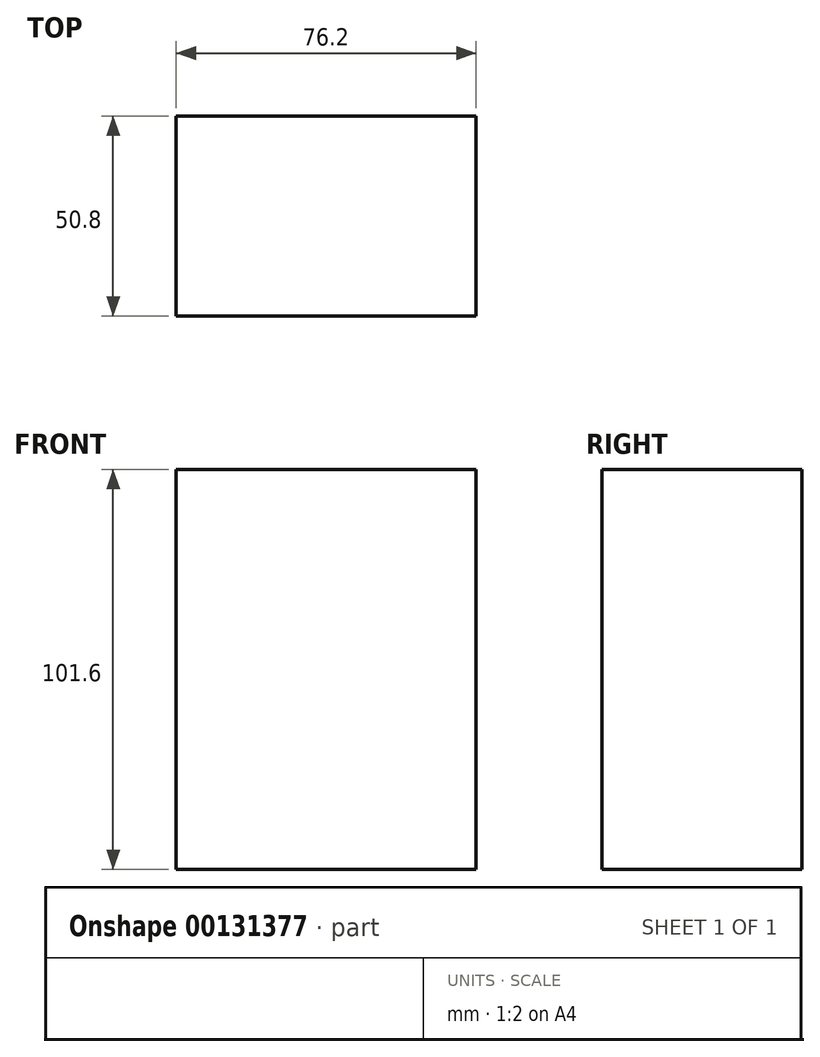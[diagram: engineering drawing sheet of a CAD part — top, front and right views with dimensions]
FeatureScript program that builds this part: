
annotation { "Feature Type Name" : "Feature", "Feature Type Description" : "" }
export const myFeature = defineFeature(function(context is Context, id is Id, definition is map)
    precondition{}
    {
        {
            var Q0;
            Q0=qCreatedBy(makeId("Front.planeOp"),FACE);
            var sketch = newSketch(context, id + "F0", { "sketchPlane" : qUnion([Q0])});
            skLineSegment(sketch, "E0.bottom", {"start": v(38.1, -50.8) * mm, "end": v(-38.1, -50.8) * mm});
            skLineSegment(sketch, "E0.top", {"start": v(38.1, 50.8) * mm, "end": v(-38.1, 50.8) * mm});
            skLineSegment(sketch, "E0.left", {"start": v(38.1, -50.8) * mm, "end": v(38.1, 50.8) * mm});
            skLineSegment(sketch, "E0.right", {"start": v(-38.1, -50.8) * mm, "end": v(-38.1, 50.8) * mm});
            skPoint(sketch, "E0.middle", {"position": v(0, 0) * mm});
            skSolve(sketch);
        }
        {
            var Q0;
            Q0 = qSketchRegion(id + "F0", true);
            extrude(context, id + "F1", {"entities" : qUnion([Q0]), "depth" : 50.8 * mm});
        }
    });
